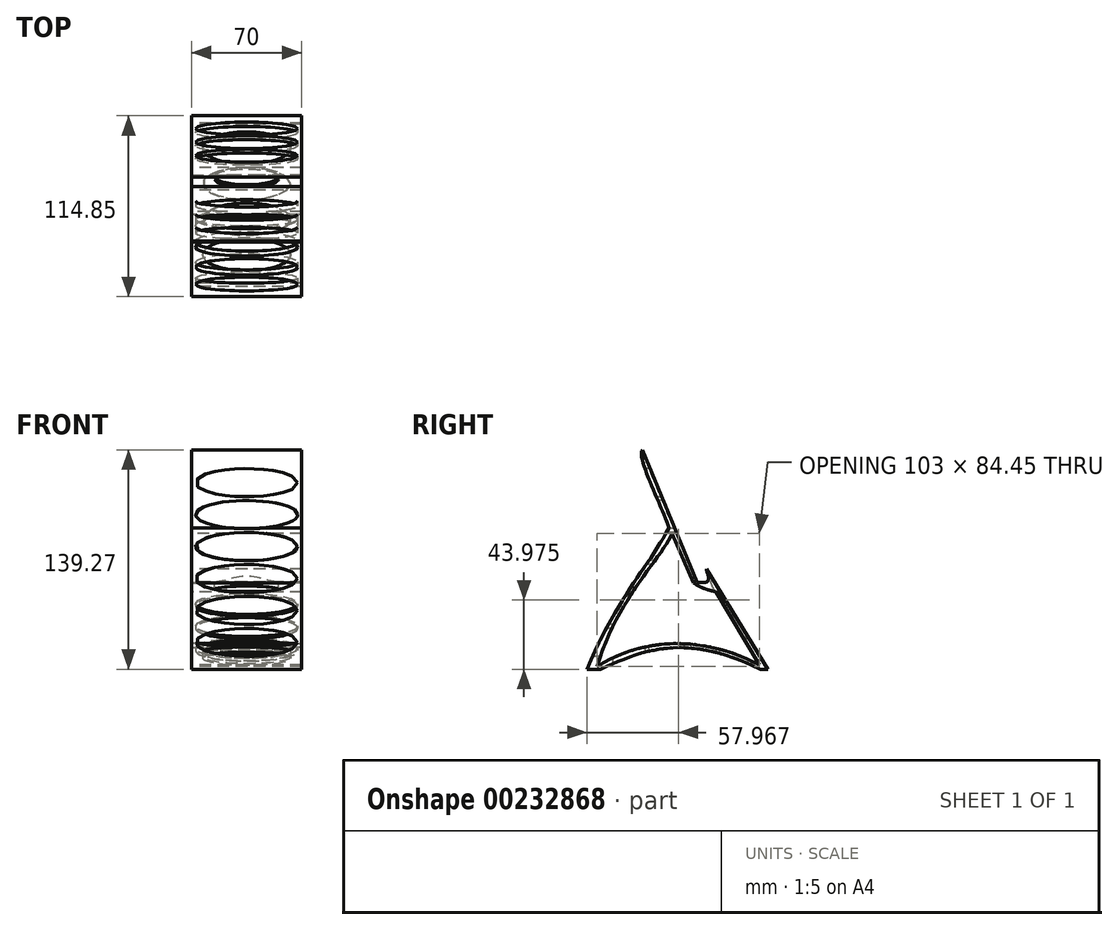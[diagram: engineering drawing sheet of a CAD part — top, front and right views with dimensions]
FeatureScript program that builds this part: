
annotation { "Feature Type Name" : "Feature", "Feature Type Description" : "" }
export const myFeature = defineFeature(function(context is Context, id is Id, definition is map)
    precondition{}
    {
        {
            var Q0;
            Q0=qCreatedBy(makeId("Right.planeOp"),FACE);
            var sketch = newSketch(context, id + "F0", { "sketchPlane" : qUnion([Q0])});
            skFitSpline(sketch, "E0", {"points": [v(-56.41, 0) * mm, v(45.2, 0) * mm], "startDerivative": vector(85.43, 39.38) * mm, "endDerivative": vector(140.76, -68.45) * mm});
            skFitSpline(sketch, "E1", {"points": [v(49.8, 0) * mm, v(10.74, 63.83) * mm], "startDerivative": vector(-39.06, 63.83) * mm, "endDerivative": vector(-39.06, 63.83) * mm});
            skLineSegment(sketch, "E2", {"start": v(-29.92, 139.27) * mm, "end": v(4.83, 55.39) * mm});
            skFitSpline(sketch, "E3", {"points": [v(-58.58, 1.75) * mm, v(-11.02, 86.2) * mm], "startDerivative": vector(35.63, 125.05) * mm, "endDerivative": vector(20.72, 47.37) * mm});
            skFitSpline(sketch, "E4", {"points": [v(-58.58, 1.75) * mm, v(44.42, 2.6) * mm], "startDerivative": vector(96.07, 60.59) * mm, "endDerivative": vector(95.42, -52.13) * mm});
            skFitSpline(sketch, "E5", {"points": [v(4.83, 55.39) * mm, v(10.74, 63.83) * mm], "startDerivative": vector(36.77, -7.47) * mm, "endDerivative": vector(2.44, 4) * mm});
            skLineSegment(sketch, "E6", {"start": v(-65.05, 0) * mm, "end": v(-56.41, 0) * mm});
            skLineSegment(sketch, "E7", {"start": v(45.2, 0) * mm, "end": v(49.8, 0) * mm});
            skLineSegment(sketch, "E8", {"start": v(16.98, 49.19) * mm, "end": v(44.42, 2.6) * mm});
            skLineSegment(sketch, "E9", {"start": v(-11.02, 86.2) * mm, "end": v(2.49, 54.83) * mm});
            skFitSpline(sketch, "E10", {"points": [v(2.49, 54.83) * mm, v(16.98, 49.19) * mm], "startDerivative": vector(13.4, -9.27) * mm, "endDerivative": vector(11.5, -1.96) * mm});
            skFitSpline(sketch, "E11", {"points": [v(-29.92, 139.27) * mm, v(-12.99, 89.65) * mm], "startDerivative": vector(-12.17, -12.55) * mm, "endDerivative": vector(13.11, -40.92) * mm});
            skFitSpline(sketch, "E12", {"points": [v(-12.99, 89.65) * mm, v(-65.05, 0) * mm], "startDerivative": vector(-40.95, -75.5) * mm, "endDerivative": vector(-59.98, -140.67) * mm});
            skSolve(sketch);
        }
        {
            var Q0;
            Q0=makeQuery(id+"F0.imprint","IMPRINT",FACE,{"disambiguationData":[TD([[makeQuery(id+"F0.imprint","IMPRINT",EDGE,{"derivedFrom":sQuery(id+"F0.wireOp",EDGE,"e2dd9e04-bce8-43ee-a2f2-a46b7d135692")}),-1.0]])]});
            var Q1;
            Q1=makeQuery(id+"F0.imprint","IMPRINT",FACE,{"disambiguationData":[TD([[makeQuery(id+"F0.imprint","IMPRINT",EDGE,{"derivedFrom":sQuery(id+"F0.wireOp",EDGE,"E0")}),1.0]])]});
            extrude(context, id + "F1", {"entities" : qUnion([Q0, Q1]), "depth" : 70 * mm});
        }
        {
            var Q0;
            Q0=makeQuery(id+"F1.opExtrude","SWEPT_FACE",FACE,{"disambiguationData":[OSD([sQuery(id+"F0.wireOp",EDGE,"E8")])]});
            var sketch = newSketch(context, id + "F2", { "sketchPlane" : qUnion([Q0])});
            skEllipse(sketch, "E13", {"center": v(35, 23.43) * mm, "majorRadius": 32.5 * mm, "minorRadius": 7.82 * mm, "majorAxis": v(1, 0)});
            skEllipse(sketch, "E14.0.1.0", {"center": v(35, 6.93) * mm, "majorRadius": 32.5 * mm, "minorRadius": 7.82 * mm, "majorAxis": v(1, 0)});
            skEllipse(sketch, "E14.0.2.0", {"center": v(35, -9.57) * mm, "majorRadius": 32.5 * mm, "minorRadius": 7.82 * mm, "majorAxis": v(1, 0)});
            skLineSegment(sketch, "E14.direction1", {"start": v(35, 23.43) * mm, "end": v(57.03, 23.43) * mm, "construction": true});
            skLineSegment(sketch, "E14.direction2", {"start": v(35, 23.43) * mm, "end": v(35, 6.93) * mm, "construction": true});
            skSolve(sketch);
        }
        {
            var Q0;
            Q0=qSketchRegion(id+"F2",true);
            var Q1;
            Q1=makeQuery(id+"F1.opExtrude","SWEPT_FACE",FACE,{"disambiguationData":[OSD([sQuery(id+"F0.wireOp",EDGE,"E1")])]});
            extrude(context, id + "F3", {"entities" : qUnion([Q0]), "operationType" : NewBodyOperationType.REMOVE, "endBound" : BoundingType.UP_TO_SURFACE, "oppositeDirection" : true, "endBoundEntityFace" : qUnion([Q1]), "depth" : 25 * mm});
        }
        {
            var Q0;
            Q0=qCreatedBy(makeId("Top.planeOp"),FACE);
            var sketch = newSketch(context, id + "F4", { "sketchPlane" : qUnion([Q0])});
            skEllipse(sketch, "E15", {"center": v(35, -38.54) * mm, "majorRadius": 27.85 * mm, "minorRadius": 10.2 * mm, "majorAxis": v(1, 0)});
            skEllipse(sketch, "E16.0.1.0", {"center": v(35, -15.94) * mm, "majorRadius": 27.85 * mm, "minorRadius": 10.2 * mm, "majorAxis": v(1, 0)});
            skEllipse(sketch, "E16.0.2.0", {"center": v(35, 6.66) * mm, "majorRadius": 27.85 * mm, "minorRadius": 10.2 * mm, "majorAxis": v(1, 0)});
            skEllipse(sketch, "E16.0.3.0", {"center": v(35, 29.26) * mm, "majorRadius": 27.85 * mm, "minorRadius": 10.2 * mm, "majorAxis": v(1, 0)});
            skLineSegment(sketch, "E16.direction1", {"start": v(35, -38.54) * mm, "end": v(60, -38.54) * mm, "construction": true});
            skLineSegment(sketch, "E16.direction2", {"start": v(35, -38.54) * mm, "end": v(35, -15.94) * mm, "construction": true});
            skSolve(sketch);
        }
        {
            var Q0;
            Q0=qSketchRegion(id+"F4",true);
            var Q1;
            Q1=makeQuery(id+"F1.opExtrude","SWEPT_FACE",FACE,{"disambiguationData":[OSD([sQuery(id+"F0.wireOp",EDGE,"E4")])]});
            extrude(context, id + "F5", {"entities" : qUnion([Q0]), "operationType" : NewBodyOperationType.REMOVE, "endBound" : BoundingType.UP_TO_SURFACE, "endBoundEntityFace" : qUnion([Q1]), "depth" : 25 * mm});
        }
        {
            var Q0;
            Q0=qCreatedBy(makeId("Front.planeOp"),FACE);
            cPlane(context, id + "F6", {"entities" : qUnion([Q0]), "cplaneType" : CPlaneType.OFFSET, "offset" : 70 * mm, "width" : 150 * mm, "height" : 150 * mm});
        }
        {
            var Q0;
            Q0=qCreatedBy(id+"F6.planeOp",FACE);
            var sketch = newSketch(context, id + "F7", { "sketchPlane" : qUnion([Q0])});
            skEllipse(sketch, "E17", {"center": v(35, 118.52) * mm, "majorRadius": 32.5 * mm, "minorRadius": 8.93 * mm, "majorAxis": v(1, 0)});
            skEllipse(sketch, "E18.0.1.0", {"center": v(35, 98.22) * mm, "majorRadius": 32.5 * mm, "minorRadius": 8.93 * mm, "majorAxis": v(1, 0)});
            skEllipse(sketch, "E18.0.2.0", {"center": v(35, 77.92) * mm, "majorRadius": 32.5 * mm, "minorRadius": 8.93 * mm, "majorAxis": v(1, 0)});
            skEllipse(sketch, "E18.0.3.0", {"center": v(35, 57.62) * mm, "majorRadius": 32.5 * mm, "minorRadius": 8.93 * mm, "majorAxis": v(1, 0)});
            skEllipse(sketch, "E18.0.4.0", {"center": v(35, 37.32) * mm, "majorRadius": 32.5 * mm, "minorRadius": 8.93 * mm, "majorAxis": v(1, 0)});
            skEllipse(sketch, "E18.0.5.0", {"center": v(35, 17.02) * mm, "majorRadius": 32.5 * mm, "minorRadius": 8.93 * mm, "majorAxis": v(1, 0)});
            skLineSegment(sketch, "E18.direction1", {"start": v(35, 118.52) * mm, "end": v(60, 118.52) * mm, "construction": true});
            skLineSegment(sketch, "E18.direction2", {"start": v(35, 118.52) * mm, "end": v(35, 98.22) * mm, "construction": true});
            skSolve(sketch);
        }
        {
            var Q0;
            Q0=makeQuery(id+"F7.imprint","IMPRINT",FACE,{"disambiguationData":[TD([[makeQuery(id+"F7.imprint","IMPRINT",EDGE,{"derivedFrom":sQuery(id+"F7.wireOp",EDGE,"E18.0.3.0")}),1.0]])]});
            var Q1;
            Q1=makeQuery(id+"F7.imprint","IMPRINT",FACE,{"disambiguationData":[TD([[makeQuery(id+"F7.imprint","IMPRINT",EDGE,{"derivedFrom":sQuery(id+"F7.wireOp",EDGE,"E18.0.4.0")}),1.0]])]});
            var Q2;
            Q2=makeQuery(id+"F7.imprint","IMPRINT",FACE,{"disambiguationData":[TD([[makeQuery(id+"F7.imprint","IMPRINT",EDGE,{"derivedFrom":sQuery(id+"F7.wireOp",EDGE,"E18.0.5.0")}),1.0]])]});
            var Q3;
            Q3=makeQuery(id+"F1.opExtrude","SWEPT_FACE",FACE,{"disambiguationData":[OSD([sQuery(id+"F0.wireOp",EDGE,"E3")])]});
            extrude(context, id + "F8", {"entities" : qUnion([Q0, Q1, Q2]), "operationType" : NewBodyOperationType.REMOVE, "endBound" : BoundingType.UP_TO_SURFACE, "oppositeDirection" : true, "endBoundEntityFace" : qUnion([Q3]), "depth" : 25 * mm});
        }
        {
            var Q0;
            Q0=makeQuery(id+"F7.imprint","IMPRINT",FACE,{"disambiguationData":[TD([[makeQuery(id+"F7.imprint","IMPRINT",EDGE,{"derivedFrom":sQuery(id+"F7.wireOp",EDGE,"E17")}),1.0]])]});
            var Q1;
            Q1=makeQuery(id+"F7.imprint","IMPRINT",FACE,{"disambiguationData":[TD([[makeQuery(id+"F7.imprint","IMPRINT",EDGE,{"derivedFrom":sQuery(id+"F7.wireOp",EDGE,"E18.0.1.0")}),1.0]])]});
            var Q2;
            Q2=makeQuery(id+"F7.imprint","IMPRINT",FACE,{"disambiguationData":[TD([[makeQuery(id+"F7.imprint","IMPRINT",EDGE,{"derivedFrom":sQuery(id+"F7.wireOp",EDGE,"E18.0.2.0")}),1.0]])]});
            var Q3;
            Q3=makeQuery(id+"F1.opExtrude","SWEPT_FACE",FACE,{"disambiguationData":[OSD([sQuery(id+"F0.wireOp",EDGE,"E2")])]});
            extrude(context, id + "F9", {"entities" : qUnion([Q0, Q1, Q2]), "operationType" : NewBodyOperationType.REMOVE, "endBound" : BoundingType.UP_TO_SURFACE, "oppositeDirection" : true, "endBoundEntityFace" : qUnion([Q3]), "depth" : 25 * mm});
        }
        {
            var Q0;
            Q0=makeQuery(id+"F1.opExtrude","SWEPT_FACE",FACE,{"disambiguationData":[OSD([sQuery(id+"F0.wireOp",EDGE,"E2")])]});
            var Q1;
            Q1=makeQuery(id+"F1.opExtrude","SWEPT_EDGE",EDGE,{"disambiguationData":[OSD([sQuery(id+"F0.wireOp",EDGE,"E2"),sQuery(id+"F0.wireOp",EDGE,"E11")])]});
            cPlane(context, id + "F10", {"entities" : qUnion([Q0, Q1]), "cplaneType" : CPlaneType.LINE_ANGLE, "offset" : 25 * mm, "angle" : 90 * degree, "width" : 150 * mm, "height" : 150 * mm});
        }
        {
            var Q0;
            Q0=qCreatedBy(id+"F10.planeOp",FACE);
            var sketch = newSketch(context, id + "F11", { "sketchPlane" : qUnion([Q0])});
            skEllipse(sketch, "E19", {"center": v(35, 29.66) * mm, "majorRadius": 20.28 * mm, "minorRadius": 4 * mm, "majorAxis": v(-1, 0)});
            skSolve(sketch);
        }
        {
            var Q0;
            Q0=qSketchRegion(id+"F11",true);
            var Q1;
            Q1=makeQuery(id+"F1.opExtrude","SWEPT_FACE",FACE,{"disambiguationData":[OSD([sQuery(id+"F0.wireOp",EDGE,"E10")])]});
            extrude(context, id + "F12", {"entities" : qUnion([Q0]), "operationType" : NewBodyOperationType.REMOVE, "endBound" : BoundingType.UP_TO_SURFACE, "oppositeDirection" : true, "endBoundEntityFace" : qUnion([Q1]), "depth" : 25 * mm});
        }
    });
